SOLIDWORKS PART (.sldprt)
format: sldprt  version: not decoded by parser v0  size: 135,680 bytes
history: native  units: mm
features: sketch x3, extrude x2, material x1, cut_extrude x1, plane x1, pattern_linear x1 (+16 scaffold rows collapsed)
feature tree (25):
  scaffold x16  (default folders/planes/origin — collapsed)
  material  "Material <not specified>"
  sketch  "Sketch1"  dims[D1=150.0mm D2=675.0mm]
  extrude  "Extrude1"  Depth=30mm
  sketch  "Sketch2"  dims[D5=24.0mm D6=24.0mm D1=75.0mm D2=75.0mm D3=625.0mm D4=625.0mm]
  cut_extrude  "Cut-Extrude1"  [1 undecoded]
  plane  "Plane1"
  sketch  "Sketch3"
  extrude  "Extrude2"  Depth=15mm
  pattern_linear  "LPattern1"  Count1=2 Count2=2 Spacing1=130mm Spacing2=130mm
decode coverage: 5 of 7 modeling features carry decoded parameters
note: 1 parameter value undecoded
note: suppression state not decoded; provenance and decode notes live in map.json
